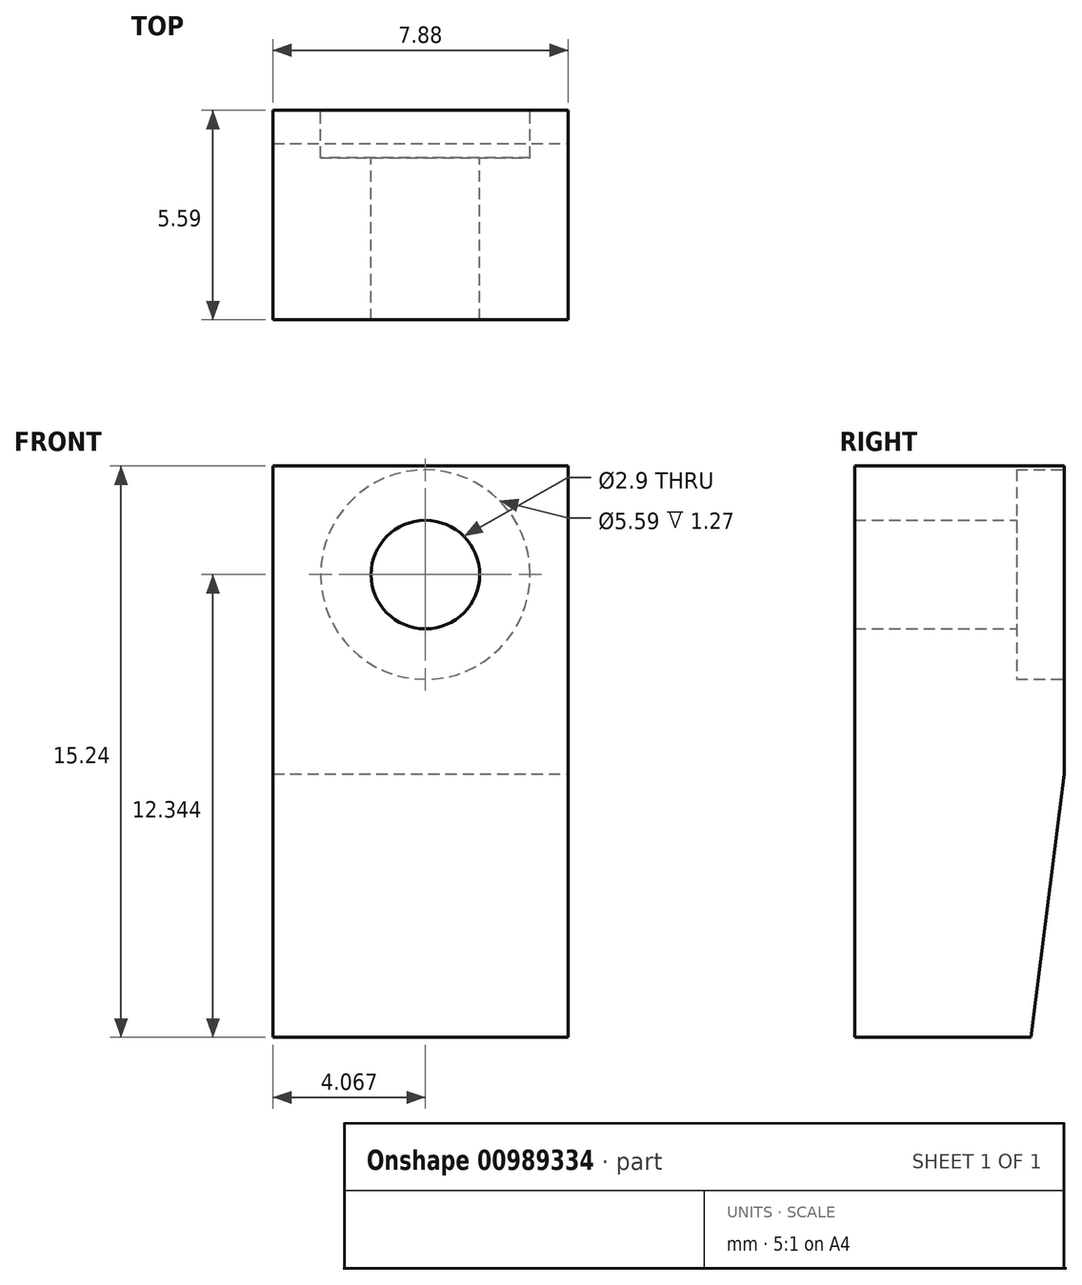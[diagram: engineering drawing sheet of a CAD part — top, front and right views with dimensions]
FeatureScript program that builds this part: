
annotation { "Feature Type Name" : "Feature", "Feature Type Description" : "" }
export const myFeature = defineFeature(function(context is Context, id is Id, definition is map)
    precondition{}
    {
        {
            var Q0;
            Q0=qCreatedBy(makeId("Front.planeOp"),FACE);
            var sketch = newSketch(context, id + "F0", { "sketchPlane" : qUnion([Q0])});
            skLineSegment(sketch, "E0.bottom", {"start": v(-108.33, 42.4) * mm, "end": v(-100.45, 42.4) * mm});
            skLineSegment(sketch, "E0.top", {"start": v(-108.33, 27.16) * mm, "end": v(-100.45, 27.16) * mm});
            skLineSegment(sketch, "E0.left", {"start": v(-108.33, 42.4) * mm, "end": v(-108.33, 27.16) * mm});
            skLineSegment(sketch, "E0.right", {"start": v(-100.45, 42.4) * mm, "end": v(-100.45, 27.16) * mm});
            skCircle(sketch, "E1", {"center": v(-104.26, 39.5) * mm, "radius": 1.45 * mm});
            skSolve(sketch);
        }
        {
            var Q0;
            Q0 = qSketchRegion(id + "F0", true);
            extrude(context, id + "F1", {"entities" : qUnion([Q0]), "depth" : 5.6 * mm, "offsetDistance" : 25.4 * mm});
        }
        {
            var Q0;
            Q0=makeQuery(id+"F1.opExtrude","CAP_FACE",FACE,{"disambiguationData":[OSD([sQuery(id+"F0.wireOp",EDGE,"E0.bottom"),sQuery(id+"F0.wireOp",EDGE,"E0.top"),sQuery(id+"F0.wireOp",EDGE,"E0.left"),sQuery(id+"F0.wireOp",EDGE,"E0.right"),sQuery(id+"F0.wireOp",EDGE,"E1")])],"isStart":true});
            var sketch = newSketch(context, id + "F2", { "sketchPlane" : qUnion([Q0])});
            skCircle(sketch, "E2", {"center": v(104.26, 39.5) * mm, "radius": 2.8 * mm});
            skSolve(sketch);
        }
        {
            var Q0;
            Q0 = qSketchRegion(id + "F2", true);
            extrude(context, id + "F3", {"entities" : qUnion([Q0]), "operationType" : NewBodyOperationType.REMOVE, "oppositeDirection" : true, "depth" : 1.27 * mm, "offsetDistance" : 25.4 * mm});
        }
        {
            var Q0;
            Q0=makeQuery(id+"F1.opExtrude","SWEPT_FACE",FACE,{"disambiguationData":[OSD([sQuery(id+"F0.wireOp",EDGE,"E0.right")])]});
            var sketch = newSketch(context, id + "F4", { "sketchPlane" : qUnion([Q0])});
            skLineSegment(sketch, "E3", {"start": v(-0.88, 27.16) * mm, "end": v(0, 34.18) * mm});
            skSolve(sketch);
        }
        {
            var Q0;
            {var subQ0=sQuery(id+"F4.wireOp",EDGE,"WiYrxY88-fWeT-LWob-deAb-qHmPPOnNKiAR");Q0=makeQuery(id+"F4.imprint","IMPRINT",FACE,{"disambiguationData":[TD([[makeQuery(id+"F4.imprint","IMPRINT",EDGE,{"derivedFrom":subQ0}),-1.0]])]});}
            var Q1;
            {var subQ0=sQuery(id+"F4.wireOp",EDGE,"E3");Q1=makeQuery(id+"F4.imprint","IMPRINT",FACE,{"disambiguationData":[TD([[makeQuery(id+"F4.imprint","IMPRINT",EDGE,{"derivedFrom":subQ0}),-1.0]])]});}
            extrude(context, id + "F5", {"entities" : qUnion([Q0, Q1]), "operationType" : NewBodyOperationType.REMOVE, "oppositeDirection" : true, "depth" : 25.4 * mm, "offsetDistance" : 25.4 * mm});
        }
    });
